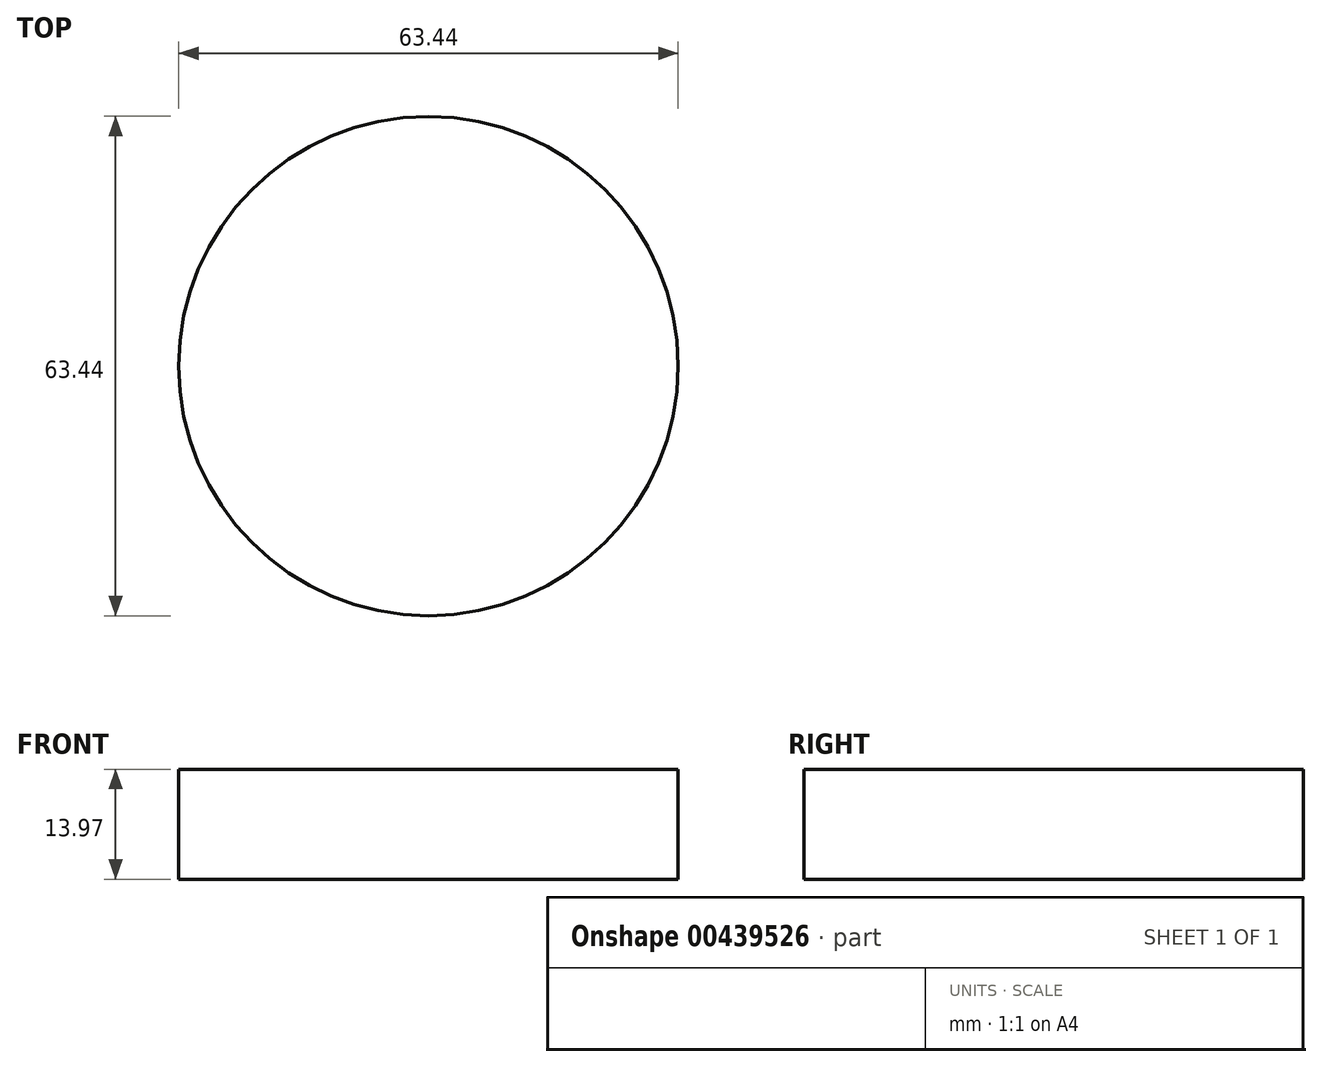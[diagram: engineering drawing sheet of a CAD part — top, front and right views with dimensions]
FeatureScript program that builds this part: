
annotation { "Feature Type Name" : "Feature", "Feature Type Description" : "" }
export const myFeature = defineFeature(function(context is Context, id is Id, definition is map)
    precondition{}
    {
        {
            var Q0;
            Q0=qCreatedBy(makeId("Top.planeOp"),FACE);
            var sketch = newSketch(context, id + "F0", { "sketchPlane" : qUnion([Q0])});
            skCircle(sketch, "E0", {"center": v(0, 6.18) * mm, "radius": 31.72 * mm});
            skSolve(sketch);
        }
        {
            var Q0;
            Q0=makeQuery(id+"F0.imprint","IMPRINT",FACE,{"disambiguationData":[TD([[makeQuery(id+"F0.imprint","IMPRINT",EDGE,{"derivedFrom":sQuery(id+"F0.wireOp",EDGE,"E0")}),1.0]])]});
            extrude(context, id + "F1", {"entities" : qUnion([Q0]), "depth" : 13.97 * mm});
        }
    });
